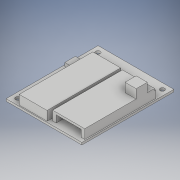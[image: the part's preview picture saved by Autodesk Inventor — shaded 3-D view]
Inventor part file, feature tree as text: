
AUTODESK INVENTOR PART (.ipt)
format: ipt  version: 2017 (Build 210142000, 142)  size: 210,432 bytes
history: native  units: in
note: dims shown in document units (in); Inventor stores cm internally (conversion verified against a paired STEP export)
features: extrude x8, sketch x8, projected_geometry x2, hole x1
ambient origin geometry x8: Origin, YZ Plane, XZ Plane, XY Plane, X Axis, Y Axis, Z Axis, Center Point
bodies: Solid1 (feature_tree)
feature tree (19):
  extrude  "Extrusion1"  Depth=2.5945in
  hole  "Hole1"  [1 undecoded]
  extrude  "Extrusion2"  Depth=0.1575in
  extrude  "Extrusion3"  Depth=0.1575in
  extrude  "Extrusion4"  Depth=0.9055in
  extrude  "Extrusion5"  Depth=0.112in
  extrude  "Extrusion6"  Depth=0.1in
  extrude  "Extrusion7"  Depth=0.1in
  extrude  "Extrusion8"  Depth=0.2in TaperAngle=0.0deg
  sketch  "Sketch1"  dims[d0=2.1378in d1=2.5945in]
  sketch  "Sketch2"  dims[d2=0.063in d3=0.0in d4=0.1654in]
  sketch  "Sketch3"  dims[d5=0.1693in d6=0.1575in]
  sketch  "Sketch4"  dims[d7=0.1654in d8=0.1575in]
  projected_geometry  "Projected Loop1"
  sketch  "Sketch5"  dims[d9=0.1693in]
  sketch  "Sketch7"  dims[d10=0.125in d11=0.75in d12=0.375in d13=0.25in d14=0.5635in d15=1.0in d16=0.8108in d17=0.9055in]
  sketch  "Sketch9"  dims[d18=2.0079in d19=0.112in]
  sketch  "Sketch10"  dims[d20=0.032in d21=0.1in d22=0.1in d23=0.2in d24=0.0in d25=0.063in d26=0.0in d27=0.315in d28=0.315in d30=0.252in d31=0.0in d32=0.2in d33=0.2992in d34=0.6811in d35=0.04in d36=0.0984in d37=0.0in d39=0.315in d40=0.4488in d41=0.035in d43=0.315in d44=0.128in d45=0.035in d46=0.3189in d47=0.0in d48=0.49in d49=0.072in d50=0.342in d51=0.027in d52=0.2165in d53=0.0in d54=1.745in d55=0.463in d56=0.952in d57=0.484in d58=0.04in d59=0.0in d60=0.5906in d61=1.563in]
  projected_geometry  "Projected Loop2"
note: 1 required parameter value undecoded (feature->parameter linkage not recoverable at this tier; creation-order binding heuristic only, values carry confidence <= 0.55)
